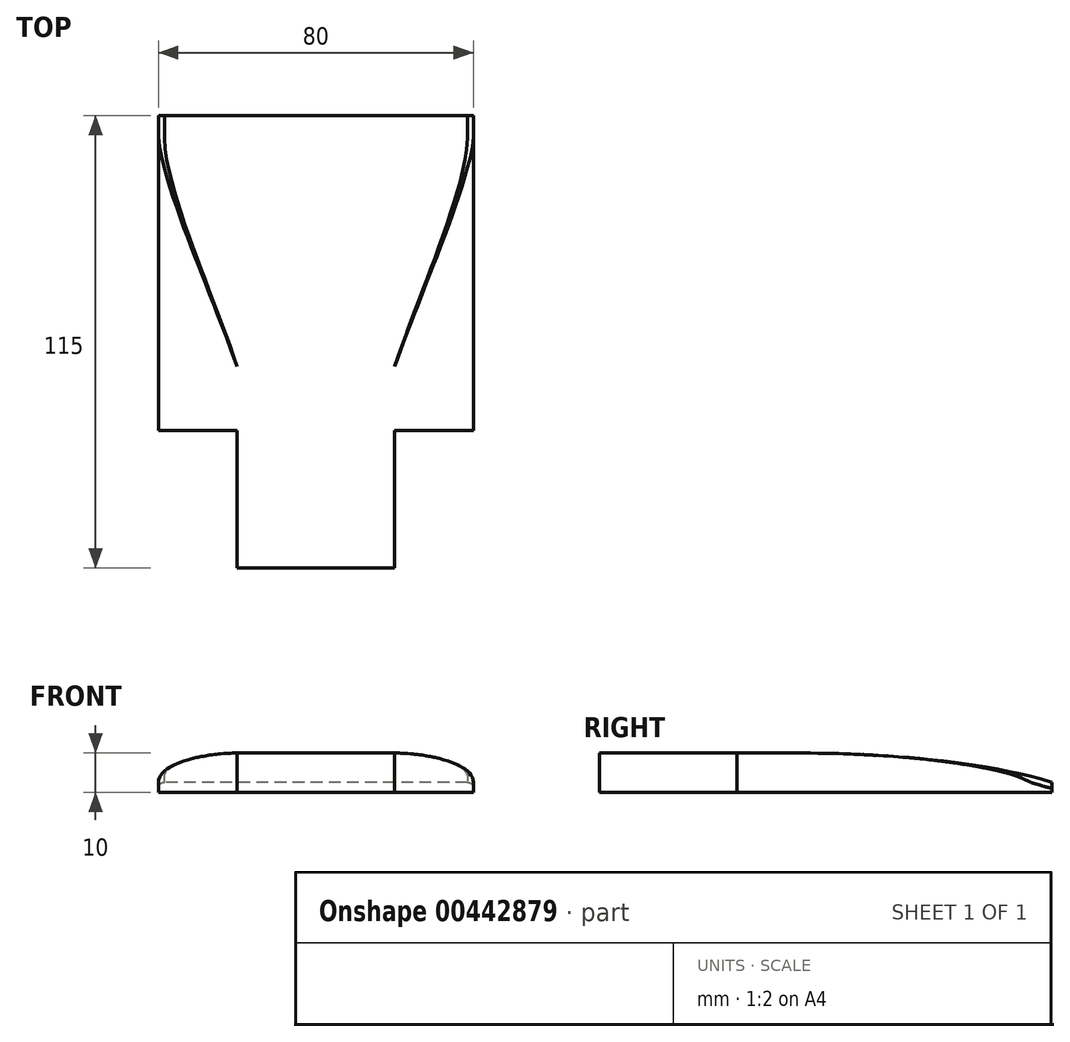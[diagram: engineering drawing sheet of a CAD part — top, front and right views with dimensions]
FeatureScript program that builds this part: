
annotation { "Feature Type Name" : "Feature", "Feature Type Description" : "" }
export const myFeature = defineFeature(function(context is Context, id is Id, definition is map)
    precondition{}
    {
        {
            var Q0;
            Q0=qCreatedBy(makeId("Top.planeOp"),FACE);
            var sketch = newSketch(context, id + "F0", { "sketchPlane" : qUnion([Q0])});
            skLineSegment(sketch, "E0.bottom", {"start": v(0, 0) * mm, "end": v(20, 0) * mm});
            skLineSegment(sketch, "E0.top", {"start": v(0, 80) * mm, "end": v(80, 80) * mm});
            skLineSegment(sketch, "E0.left", {"start": v(0, 0) * mm, "end": v(0, 80) * mm});
            skLineSegment(sketch, "E0.right", {"start": v(80, 0) * mm, "end": v(80, 80) * mm});
            skLineSegment(sketch, "E1", {"start": v(40, 0) * mm, "end": v(40, -25.9) * mm, "construction": true});
            skLineSegment(sketch, "E2.top", {"start": v(60, -35) * mm, "end": v(20, -35) * mm});
            skLineSegment(sketch, "E2.left", {"start": v(60, 0) * mm, "end": v(60, -35) * mm});
            skLineSegment(sketch, "E2.right", {"start": v(20, 0) * mm, "end": v(20, -35) * mm});
            skPoint(sketch, "E2.middle", {"position": v(40, -17.5) * mm});
            skLineSegment(sketch, "E3.trimOffspring", {"start": v(60, 0) * mm, "end": v(80, 0) * mm});
            skSolve(sketch);
        }
        {
            var Q0;
            Q0=makeQuery(id+"F0.imprint","IMPRINT",FACE,{"disambiguationData":[TD([[makeQuery(id+"F0.imprint","IMPRINT",EDGE,{"derivedFrom":sQuery(id+"F0.wireOp",EDGE,"E0.bottom")}),1.0]])]});
            extrude(context, id + "F1", {"entities" : qUnion([Q0]), "depth" : 10 * mm});
        }
        {
            var Q0;
            Q0=makeQuery(id+"F1.opExtrude","SWEPT_FACE",FACE,{"disambiguationData":[OSD([sQuery(id+"F0.wireOp",EDGE,"E0.left")])]});
            var sketch = newSketch(context, id + "F2", { "sketchPlane" : qUnion([Q0])});
            skFitSpline(sketch, "E4", {"points": [v(-80, 2.54) * mm, v(-16.18, 10) * mm], "startDerivative": vector(40.66, 13.27) * mm, "endDerivative": vector(77.5, 0) * mm});
            skLineSegment(sketch, "E5", {"start": v(-80, 2.54) * mm, "end": v(-90.72, 5.94) * mm});
            skLineSegment(sketch, "E6", {"start": v(-90.72, 5.94) * mm, "end": v(-81.1, 20.64) * mm});
            skLineSegment(sketch, "E7", {"start": v(-81.1, 20.64) * mm, "end": v(-16.18, 10) * mm});
            skSolve(sketch);
        }
        {
            var Q0;
            {var subQ0=sQuery(id+"F2.wireOp",EDGE,"E4");Q0=makeQuery(id+"F2.imprint","IMPRINT",FACE,{"disambiguationData":[TD([[makeQuery(id+"F2.imprint","IMPRINT",EDGE,{"derivedFrom":subQ0}),1.0]])]});}
            extrude(context, id + "F3", {"entities" : qUnion([Q0]), "operationType" : NewBodyOperationType.REMOVE, "oppositeDirection" : true, "depth" : 134.7 * mm});
        }
        {
            var Q0;
            Q0=makeQuery(id+"F1.opExtrude","SWEPT_FACE",FACE,{"disambiguationData":[OSD([sQuery(id+"F0.wireOp",EDGE,"E3.trimOffspring")])]});
            var sketch = newSketch(context, id + "F4", { "sketchPlane" : qUnion([Q0])});
            skLineSegment(sketch, "E8", {"start": v(80, 0) * mm, "end": v(0, 0) * mm, "construction": true});
            skLineSegment(sketch, "E9", {"start": v(40, 0) * mm, "end": v(40, 17.5) * mm, "construction": true});
            skPoint(sketch, "E9.endSnap0", {"position": v(40, 0) * mm});
            skFitSpline(sketch, "E10", {"points": [v(60, 10) * mm, v(80, 2.54) * mm], "startDerivative": vector(23.95, 0) * mm, "endDerivative": vector(0, -15.04) * mm});
            skFitSpline(sketch, "E11.MirrorCS", {"points": [v(20, 10) * mm, v(0, 2.54) * mm], "startDerivative": vector(-23.95, 0) * mm, "endDerivative": vector(0, -15.04) * mm});
            skLineSegment(sketch, "E12", {"start": v(0, 2.54) * mm, "end": v(0, 10) * mm});
            skLineSegment(sketch, "E13", {"start": v(0, 10) * mm, "end": v(20, 10) * mm});
            skLineSegment(sketch, "E14", {"start": v(80, 2.54) * mm, "end": v(80, 10) * mm});
            skLineSegment(sketch, "E15", {"start": v(80, 10) * mm, "end": v(60, 10) * mm});
            skPoint(sketch, "E16", {"position": v(80, 5) * mm});
            skSolve(sketch);
        }
        {
            var Q0;
            Q0=makeQuery(id+"F4.imprint","IMPRINT",FACE,{"disambiguationData":[TD([[makeQuery(id+"F4.imprint","IMPRINT",EDGE,{"derivedFrom":sQuery(id+"F4.wireOp",EDGE,"E10")}),1.0]])]});
            var Q1;
            Q1=makeQuery(id+"F4.imprint","IMPRINT",FACE,{"disambiguationData":[TD([[makeQuery(id+"F4.imprint","IMPRINT",EDGE,{"derivedFrom":sQuery(id+"F4.wireOp",EDGE,"E11.MirrorCS")}),-1.0]])]});
            extrude(context, id + "F5", {"entities" : qUnion([Q0, Q1]), "operationType" : NewBodyOperationType.REMOVE, "oppositeDirection" : true, "depth" : 148 * mm});
        }
        {
            var Q0;
            Q0=makeQuery(id+"F5.boolean.opBoolean","INTERSECT",EDGE,{"derivedFrom":[makeQuery(id+"F3.boolean.opBoolean","COPY",FACE,{"derivedFrom":makeQuery(id+"F3.opExtrude","SWEPT_FACE",FACE,{"disambiguationData":[OSD([sQuery(id+"F2.wireOp",EDGE,"E4")])]})}),makeQuery(id+"F5.opExtrude","SWEPT_FACE",FACE,{"disambiguationData":[OSD([sQuery(id+"F4.wireOp",EDGE,"E11.MirrorCS")])]})]});
            var Q1;
            Q1=makeQuery(id+"F5.boolean.opBoolean","INTERSECT",EDGE,{"derivedFrom":[makeQuery(id+"F3.boolean.opBoolean","COPY",FACE,{"derivedFrom":makeQuery(id+"F3.opExtrude","SWEPT_FACE",FACE,{"disambiguationData":[OSD([sQuery(id+"F2.wireOp",EDGE,"E4")])]})}),makeQuery(id+"F5.opExtrude","SWEPT_FACE",FACE,{"disambiguationData":[OSD([sQuery(id+"F4.wireOp",EDGE,"E10")])]})]});
            fillet(context, id + "F6", {"entities" : qUnion([Q0, Q1]), "radius" : 1.5 * mm, "rho" : 0.5, "crossSection" : FilletCrossSection.CONIC, "allowEdgeOverflow" : false});
        }
    });
